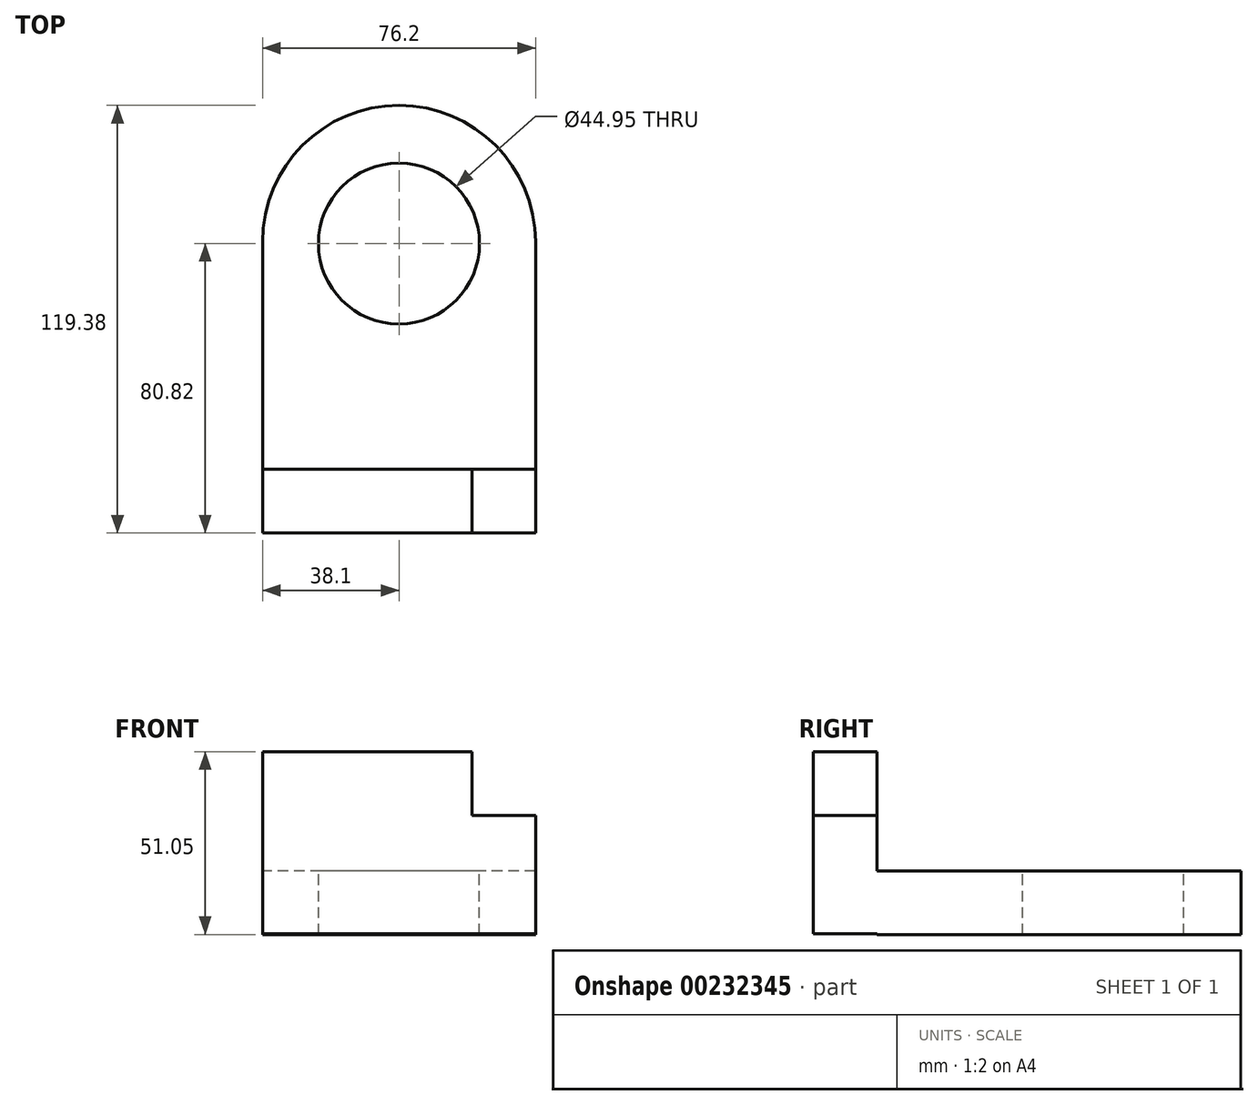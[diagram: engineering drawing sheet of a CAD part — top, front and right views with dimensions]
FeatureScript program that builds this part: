
annotation { "Feature Type Name" : "Feature", "Feature Type Description" : "" }
export const myFeature = defineFeature(function(context is Context, id is Id, definition is map)
    precondition{}
    {
        {
            var Q0;
            Q0=qCreatedBy(makeId("Front.planeOp"),FACE);
            var sketch = newSketch(context, id + "F0", { "sketchPlane" : qUnion([Q0])});
            skLineSegment(sketch, "E0.bottom", {"start": v(38.1, -25.4) * mm, "end": v(-38.1, -25.4) * mm});
            skLineSegment(sketch, "E0.top", {"start": v(38.1, 25.4) * mm, "end": v(-38.1, 25.4) * mm});
            skLineSegment(sketch, "E0.left", {"start": v(38.1, -25.4) * mm, "end": v(38.1, 25.4) * mm});
            skLineSegment(sketch, "E0.right", {"start": v(-38.1, -25.4) * mm, "end": v(-38.1, 25.4) * mm});
            skPoint(sketch, "E0.middle", {"position": v(0, 0) * mm});
            skLineSegment(sketch, "E1.bottom", {"start": v(38.1, 25.4) * mm, "end": v(20.32, 25.4) * mm});
            skLineSegment(sketch, "E1.top", {"start": v(38.1, 7.62) * mm, "end": v(20.32, 7.62) * mm});
            skLineSegment(sketch, "E1.left", {"start": v(38.1, 25.4) * mm, "end": v(38.1, 7.62) * mm});
            skLineSegment(sketch, "E1.right", {"start": v(20.32, 25.4) * mm, "end": v(20.32, 7.62) * mm});
            skSolve(sketch);
        }
        {
            var Q0;
            Q0=makeQuery(id+"F0.imprint","IMPRINT",FACE,{"disambiguationData":[TD([[makeQuery(id+"F0.imprint","IMPRINT",EDGE,{"derivedFrom":sQuery(id+"F0.wireOp",EDGE,"E0.bottom")}),-1.0]])]});
            extrude(context, id + "F1", {"entities" : qUnion([Q0]), "depth" : 17.78 * mm});
        }
        {
            var Q0;
            Q0=qCreatedBy(makeId("Right.planeOp"),FACE);
            var sketch = newSketch(context, id + "F2", { "sketchPlane" : qUnion([Q0])});
            skLineSegment(sketch, "E2.bottom", {"start": v(0, -25.65) * mm, "end": v(101.6, -25.65) * mm});
            skLineSegment(sketch, "E2.top", {"start": v(0, -7.87) * mm, "end": v(101.6, -7.87) * mm});
            skLineSegment(sketch, "E2.left", {"start": v(0, -25.65) * mm, "end": v(0, -7.87) * mm});
            skLineSegment(sketch, "E2.right", {"start": v(101.6, -25.65) * mm, "end": v(101.6, -7.87) * mm});
            skSolve(sketch);
        }
        {
            var Q0;
            Q0=makeQuery(id+"F2.imprint","IMPRINT",FACE,{"disambiguationData":[TD([[makeQuery(id+"F2.imprint","IMPRINT",EDGE,{"derivedFrom":sQuery(id+"F2.wireOp",EDGE,"E2.bottom")}),1.0]])]});
            extrude(context, id + "F3", {"entities" : qUnion([Q0]), "operationType" : NewBodyOperationType.ADD, "depth" : 38.1 * mm});
        }
        {
            var Q0;
            Q0=makeQuery(id+"F3.opExtrude","CAP_FACE",FACE,{"disambiguationData":[OSD([sQuery(id+"F2.wireOp",EDGE,"E2.bottom"),sQuery(id+"F2.wireOp",EDGE,"E2.top"),sQuery(id+"F2.wireOp",EDGE,"E2.left"),sQuery(id+"F2.wireOp",EDGE,"E2.right")])],"isStart":true});
            extrude(context, id + "F4", {"entities" : qUnion([Q0]), "operationType" : NewBodyOperationType.ADD, "depth" : 38.1 * mm});
        }
        {
            var Q0;
            {var subQ0=sQuery(id+"F2.wireOp",EDGE,"E2.top");Q0=makeQuery(id+"F4.boolean.opBoolean","MERGE",FACE,{"derivedFrom":[makeQuery(id+"F3.opExtrude","SWEPT_FACE",FACE,{"disambiguationData":[OSD([subQ0])]}),makeQuery(id+"F4.opExtrude","SWEPT_FACE",FACE,{"disambiguationData":[OSD([subQ0])]})]});}
            var sketch = newSketch(context, id + "F5", { "sketchPlane" : qUnion([Q0])});
            skCircle(sketch, "E3", {"center": v(0, 63.5) * mm, "radius": 38.1 * mm});
            skSolve(sketch);
        }
        {
            var Q0;
            Q0=qCreatedBy(makeId("Top.planeOp"),FACE);
            var sketch = newSketch(context, id + "F6", { "sketchPlane" : qUnion([Q0])});
            skCircle(sketch, "E4", {"center": v(0, 63.04) * mm, "radius": 22.48 * mm});
            skSolve(sketch);
        }
        {
            var Q0;
            Q0=makeQuery(id+"F6.imprint","IMPRINT",FACE,{"disambiguationData":[TD([[makeQuery(id+"F6.imprint","IMPRINT",EDGE,{"derivedFrom":sQuery(id+"F6.wireOp",EDGE,"E4")}),1.0]])]});
            extrude(context, id + "F7", {"entities" : qUnion([Q0]), "operationType" : NewBodyOperationType.REMOVE, "oppositeDirection" : true, "depth" : 50.8 * mm});
        }
        {
            var Q0;
            {var subQ0=sQuery(id+"F5.wireOp",EDGE,"E3");var subQ2=sQuery(id+"F2.wireOp",EDGE,"E2.top");var subQ5=makeQuery(id+"F3.opExtrude","CAP_EDGE",EDGE,{"disambiguationData":[OSD([subQ2])],"isStart":false});var subQ6=makeQuery(id+"F5.imprint","INTERSECT",VERTEX,{"derivedFrom":[subQ5,subQ0]});Q0=makeQuery(id+"F5.imprint","IMPRINT",FACE,{"disambiguationData":[TD([[makeQuery(id+"F5.imprint","IMPRINT",EDGE,{"disambiguationData":[TD([[subQ6,-1.0]])],"derivedFrom":subQ0}),-1.0]])]});}
            extrude(context, id + "F8", {"entities" : qUnion([Q0]), "operationType" : NewBodyOperationType.REMOVE, "oppositeDirection" : true, "depth" : 50.8 * mm});
        }
        {
            var Q0;
            {var subQ0=sQuery(id+"F5.wireOp",EDGE,"E3");var subQ2=sQuery(id+"F2.wireOp",EDGE,"E2.top");var subQ5=makeQuery(id+"F4.opExtrude","CAP_EDGE",EDGE,{"disambiguationData":[OSD([subQ2])],"isStart":false});var subQ6=makeQuery(id+"F5.imprint","INTERSECT",VERTEX,{"derivedFrom":[subQ5,subQ0]});Q0=makeQuery(id+"F5.imprint","IMPRINT",FACE,{"disambiguationData":[TD([[makeQuery(id+"F5.imprint","IMPRINT",EDGE,{"disambiguationData":[TD([[subQ6,1.0]])],"derivedFrom":subQ0}),-1.0]])]});}
            extrude(context, id + "F9", {"entities" : qUnion([Q0]), "operationType" : NewBodyOperationType.REMOVE, "oppositeDirection" : true, "depth" : 50.8 * mm});
        }
    });
